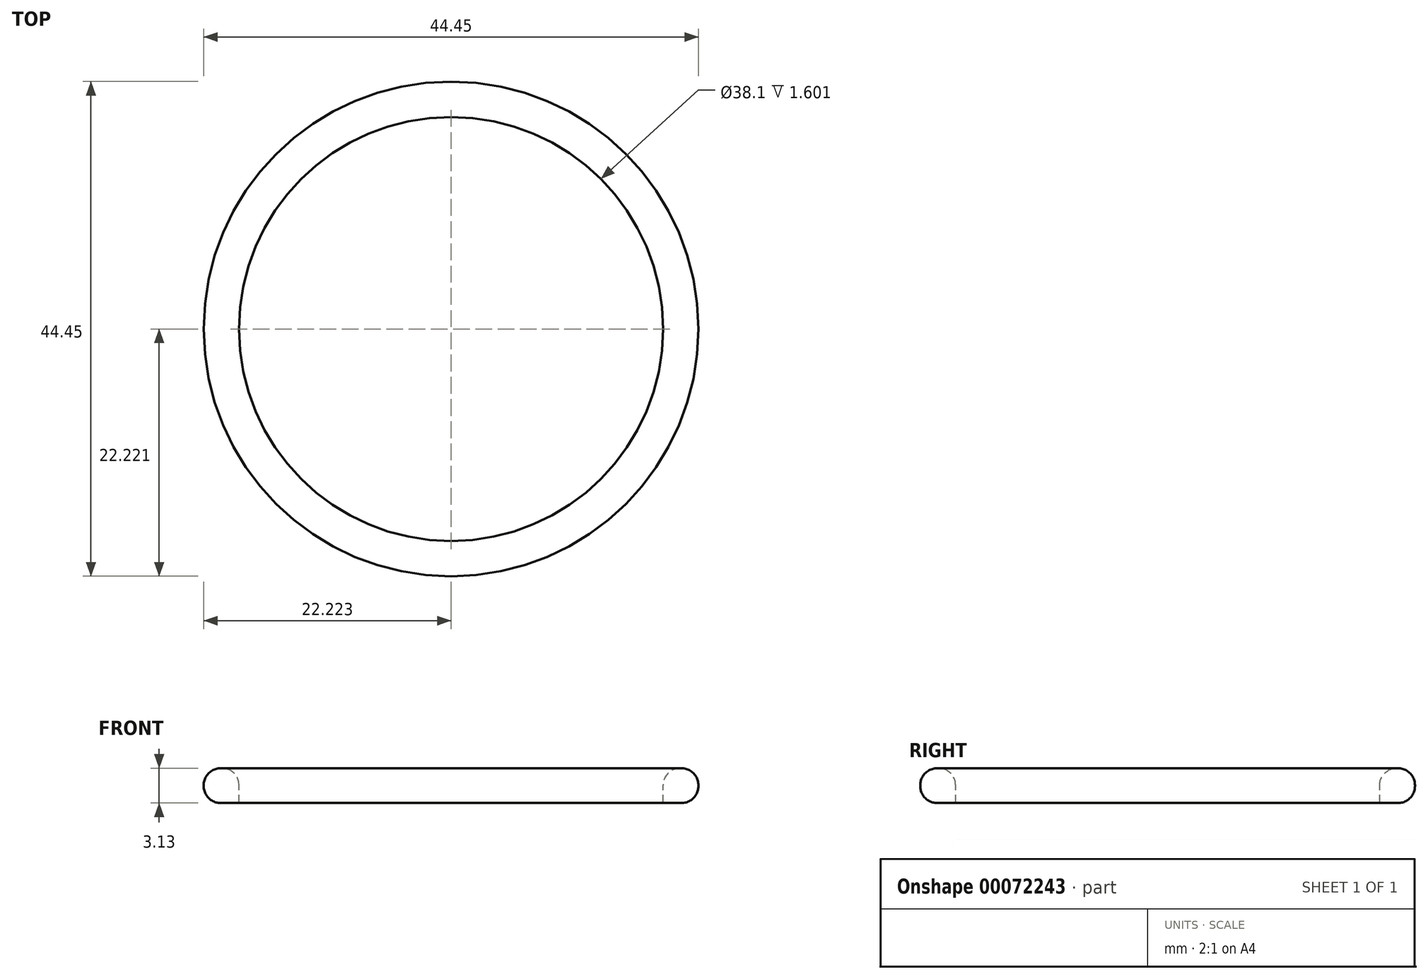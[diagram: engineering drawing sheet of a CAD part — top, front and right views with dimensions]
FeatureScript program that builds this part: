
annotation { "Feature Type Name" : "Feature", "Feature Type Description" : "" }
export const myFeature = defineFeature(function(context is Context, id is Id, definition is map)
    precondition{}
    {
        {
            var Q0;
            Q0=qCreatedBy(makeId("Top.planeOp"),FACE);
            var sketch = newSketch(context, id + "F0", { "sketchPlane" : qUnion([Q0])});
            skCircle(sketch, "E0", {"center": v(-3.07, 6.4) * mm, "radius": 22.23 * mm});
            skSolve(sketch);
        }
        {
            var Q0;
            Q0=makeQuery(id+"F0.imprint","IMPRINT",FACE,{"disambiguationData":[TD([[makeQuery(id+"F0.imprint","IMPRINT",EDGE,{"derivedFrom":sQuery(id+"F0.wireOp",EDGE,"E0")}),1.0]])]});
            var Q1;
            Q1=makeQuery(id+"F0.imprint","IMPRINT",FACE,{"disambiguationData":[TD([[makeQuery(id+"F0.imprint","IMPRINT",EDGE,{"derivedFrom":sQuery(id+"F0.wireOp",EDGE,"97eacbc2-6655-49a0-91dd-b539d5c7cae5")}),1.0]])]});
            extrude(context, id + "F1", {"entities" : qUnion([Q0, Q1]), "depth" : ((2 / 16) * 25) * mm});
        }
        {
            var Q0;
            Q0=makeQuery(id+"F1.opExtrude","CAP_FACE",FACE,{"disambiguationData":[OSD([sQuery(id+"F0.wireOp",EDGE,"E0")])],"isStart":false});
            var sketch = newSketch(context, id + "F2", { "sketchPlane" : qUnion([Q0])});
            skCircle(sketch, "E1", {"center": v(-3.07, 6.4) * mm, "radius": 19.05 * mm});
            skSolve(sketch);
        }
        {
            var Q0;
            Q0 = qSketchRegion(id + "F2", true);
            extrude(context, id + "F3", {"entities" : qUnion([Q0]), "operationType" : NewBodyOperationType.REMOVE, "endBound" : BoundingType.THROUGH_ALL, "oppositeDirection" : true, "depth" : ((1 / 8) * 24) * mm});
        }
        {
            var Q0;
            Q0=makeQuery(id+"F1.opExtrude","SWEPT_FACE",FACE,{"disambiguationData":[OSD([sQuery(id+"F0.wireOp",EDGE,"E0")])]});
            var Q1;
            Q1=makeQuery(id+"F1.opExtrude","CAP_FACE",FACE,{"disambiguationData":[OSD([sQuery(id+"F0.wireOp",EDGE,"E0")])],"isStart":false});
            fillet(context, id + "F4", {"entities" : qUnion([Q0, Q1]), "radius" : 1.52 * mm, "tangentPropagation" : true, "allowEdgeOverflow" : false});
        }
    });
